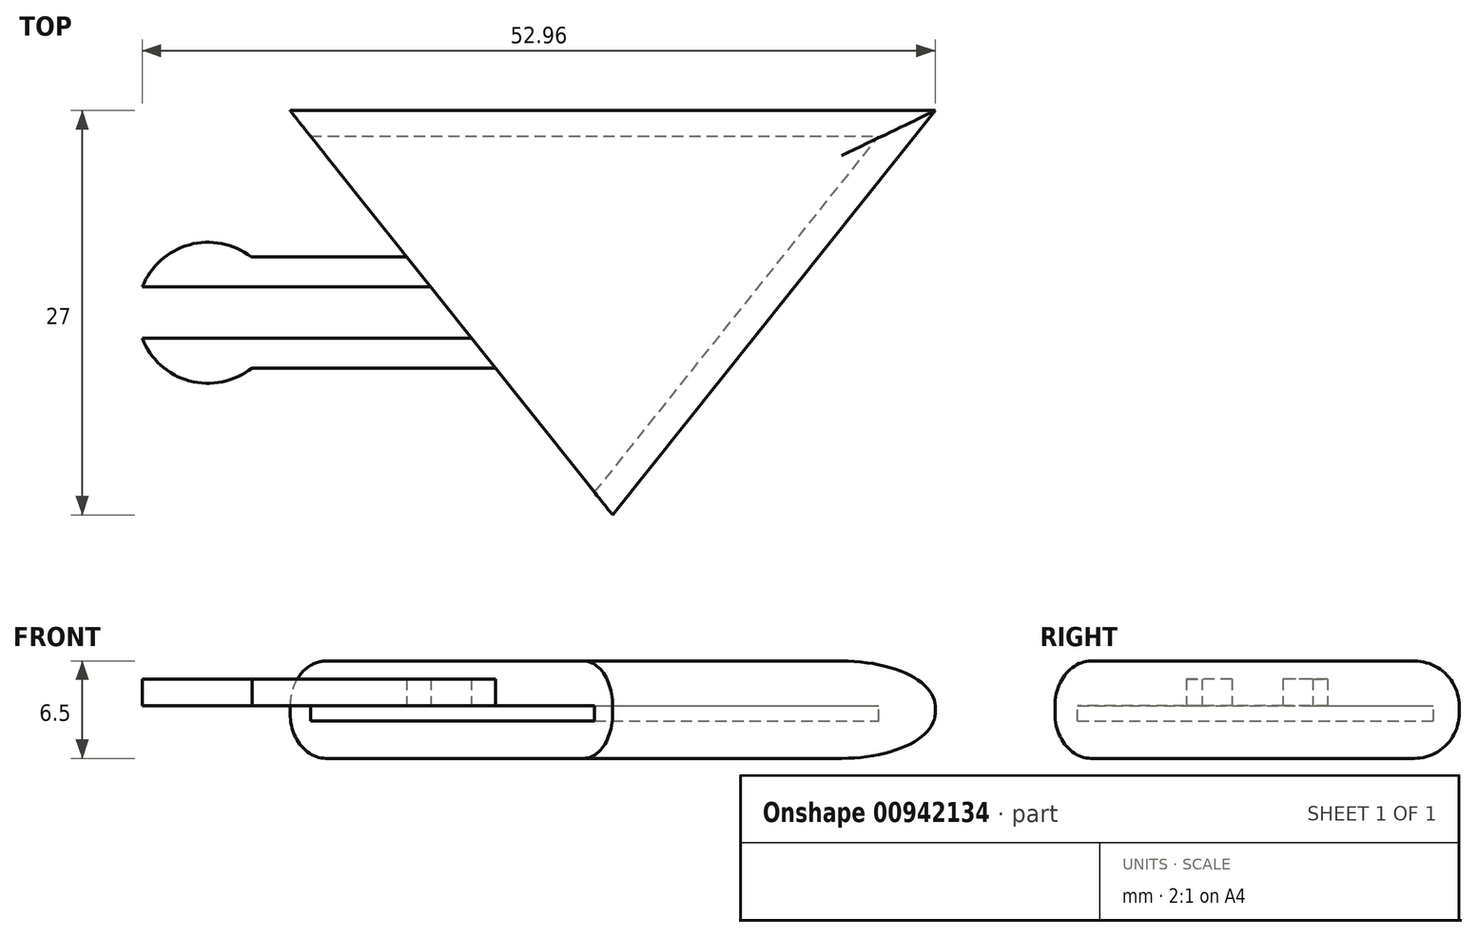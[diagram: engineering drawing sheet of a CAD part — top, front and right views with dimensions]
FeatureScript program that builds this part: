
annotation { "Feature Type Name" : "Feature", "Feature Type Description" : "" }
export const myFeature = defineFeature(function(context is Context, id is Id, definition is map)
    precondition{}
    {
        {
            var Q0;
            Q0=qCreatedBy(makeId("Top.planeOp"),FACE);
            var sketch = newSketch(context, id + "F0", { "sketchPlane" : qUnion([Q0])});
            skCircle(sketch, "E0", {"center": v(0, 0) * mm, "radius": 5 * mm, "construction": true});
            skLineSegment(sketch, "E1", {"start": v(3, 4) * mm, "end": v(13.09, 4) * mm, "construction": true});
            skLineSegment(sketch, "E2", {"start": v(3, -4) * mm, "end": v(19.42, -4) * mm, "construction": true});
            skLineSegment(sketch, "E3", {"start": v(19.42, -4) * mm, "end": v(13.09, 4) * mm, "construction": true});
            skLineSegment(sketch, "E4.MirrorCS", {"start": v(27.02, -13.5) * mm, "end": v(-5.48, -13.5) * mm, "construction": true});
            skLineSegment(sketch, "E5.MirrorCS", {"start": v(5.48, 13.5) * mm, "end": v(27.02, -13.5) * mm, "construction": true});
            skLineSegment(sketch, "E6.MirrorCS", {"start": v(-27.02, 13.5) * mm, "end": v(5.48, 13.5) * mm, "construction": true});
            skLineSegment(sketch, "E7.MirrorCS", {"start": v(-27.02, 13.5) * mm, "end": v(-5.48, -13.5) * mm, "construction": true});
            skLineSegment(sketch, "E8", {"start": v(5.48, 13.5) * mm, "end": v(48.56, 13.5) * mm, "construction": true});
            skLineSegment(sketch, "E9", {"start": v(48.56, 13.5) * mm, "end": v(27.02, -13.5) * mm, "construction": true});
            skLineSegment(sketch, "E10", {"start": v(6.85, 11.79) * mm, "end": v(44.8, 11.79) * mm, "construction": true});
            skLineSegment(sketch, "E11", {"start": v(44.8, 11.79) * mm, "end": v(25.82, -12) * mm, "construction": true});
            skSolve(sketch);
        }
        {
            var Q0;
            Q0=qCreatedBy(makeId("Top.planeOp"),FACE);
            var sketch = newSketch(context, id + "F1", { "sketchPlane" : qUnion([Q0])});
            skCircle(sketch, "E12", {"center": v(0, 0) * mm, "radius": 5 * mm, "construction": true});
            skLineSegment(sketch, "E13", {"start": v(3, 4) * mm, "end": v(13.09, 4) * mm, "construction": true});
            skLineSegment(sketch, "E14", {"start": v(3, -4) * mm, "end": v(19.42, -4) * mm, "construction": true});
            skLineSegment(sketch, "E15", {"start": v(19.42, -4) * mm, "end": v(13.09, 4) * mm, "construction": true});
            skLineSegment(sketch, "E16.MirrorCS", {"start": v(27.02, -13.5) * mm, "end": v(-5.48, -13.5) * mm, "construction": true});
            skLineSegment(sketch, "E17.MirrorCS", {"start": v(5.48, 13.5) * mm, "end": v(27.02, -13.5) * mm, "construction": true});
            skLineSegment(sketch, "E18.MirrorCS", {"start": v(-27.02, 13.5) * mm, "end": v(5.48, 13.5) * mm, "construction": true});
            skLineSegment(sketch, "E19.MirrorCS", {"start": v(-27.02, 13.5) * mm, "end": v(-5.48, -13.5) * mm, "construction": true});
            skLineSegment(sketch, "E20", {"start": v(5.48, 13.5) * mm, "end": v(48.56, 13.5) * mm, "construction": true});
            skLineSegment(sketch, "E21", {"start": v(48.56, 13.5) * mm, "end": v(27.02, -13.5) * mm, "construction": true});
            skLineSegment(sketch, "E22", {"start": v(6.85, 11.79) * mm, "end": v(44.8, 11.79) * mm, "construction": true});
            skLineSegment(sketch, "E23", {"start": v(44.8, 11.79) * mm, "end": v(25.82, -12) * mm, "construction": true});
            skLineSegment(sketch, "E24", {"start": v(5.48, 13.5) * mm, "end": v(27.02, -13.5) * mm});
            skLineSegment(sketch, "E25", {"start": v(48.56, 13.5) * mm, "end": v(5.48, 13.5) * mm});
            skLineSegment(sketch, "E26", {"start": v(48.56, 13.5) * mm, "end": v(27.02, -13.5) * mm});
            skSolve(sketch);
        }
        {
            var Q0;
            Q0=makeQuery(id+"F1.imprint","IMPRINT",FACE,{"disambiguationData":[TD([[makeQuery(id+"F1.imprint","IMPRINT",EDGE,{"derivedFrom":sQuery(id+"F1.wireOp",EDGE,"E24")}),1.0]])]});
            extrude(context, id + "F2", {"entities" : qUnion([Q0]), "oppositeDirection" : true, "depth" : 3.5 * mm, "offsetDistance" : 25 * mm});
        }
        {
            var Q0;
            Q0=qCreatedBy(makeId("Top.planeOp"),FACE);
            var sketch = newSketch(context, id + "F3", { "sketchPlane" : qUnion([Q0])});
            skCircle(sketch, "E27", {"center": v(0, 0) * mm, "radius": 5 * mm, "construction": true});
            skLineSegment(sketch, "E28", {"start": v(3, 4) * mm, "end": v(13.09, 4) * mm, "construction": true});
            skLineSegment(sketch, "E29", {"start": v(3, -4) * mm, "end": v(19.42, -4) * mm, "construction": true});
            skLineSegment(sketch, "E30", {"start": v(19.42, -4) * mm, "end": v(13.09, 4) * mm, "construction": true});
            skLineSegment(sketch, "E31.MirrorCS", {"start": v(27.02, -13.5) * mm, "end": v(-5.48, -13.5) * mm, "construction": true});
            skLineSegment(sketch, "E32.MirrorCS", {"start": v(5.48, 13.5) * mm, "end": v(27.02, -13.5) * mm, "construction": true});
            skLineSegment(sketch, "E33.MirrorCS", {"start": v(-27.02, 13.5) * mm, "end": v(5.48, 13.5) * mm, "construction": true});
            skLineSegment(sketch, "E34.MirrorCS", {"start": v(-27.02, 13.5) * mm, "end": v(-5.48, -13.5) * mm, "construction": true});
            skLineSegment(sketch, "E35", {"start": v(5.48, 13.5) * mm, "end": v(48.56, 13.5) * mm, "construction": true});
            skLineSegment(sketch, "E36", {"start": v(48.56, 13.5) * mm, "end": v(27.02, -13.5) * mm, "construction": true});
            skLineSegment(sketch, "E37", {"start": v(6.85, 11.79) * mm, "end": v(44.8, 11.79) * mm, "construction": true});
            skLineSegment(sketch, "E38", {"start": v(44.8, 11.79) * mm, "end": v(25.82, -12) * mm, "construction": true});
            skLineSegment(sketch, "E39", {"start": v(6.85, 11.79) * mm, "end": v(44.8, 11.79) * mm});
            skLineSegment(sketch, "E40", {"start": v(25.82, -12) * mm, "end": v(44.8, 11.79) * mm});
            skLineSegment(sketch, "E41", {"start": v(25.82, -12) * mm, "end": v(6.85, 11.79) * mm});
            skSolve(sketch);
        }
        {
            var Q0;
            Q0=makeQuery(id+"F3.imprint","IMPRINT",FACE,{"disambiguationData":[TD([[makeQuery(id+"F3.imprint","IMPRINT",EDGE,{"derivedFrom":sQuery(id+"F3.wireOp",EDGE,"E39")}),-1.0]])]});
            extrude(context, id + "F4", {"entities" : qUnion([Q0]), "operationType" : NewBodyOperationType.REMOVE, "oppositeDirection" : true, "depth" : 1 * mm, "offsetDistance" : 25 * mm});
        }
        {
            var Q0;
            Q0=makeQuery(id+"F2.opExtrude","CAP_FACE",FACE,{"disambiguationData":[OSD([sQuery(id+"F1.wireOp",EDGE,"E24"),sQuery(id+"F1.wireOp",EDGE,"E25"),sQuery(id+"F1.wireOp",EDGE,"E26")])],"isStart":true});
            var sketch = newSketch(context, id + "F5", { "sketchPlane" : qUnion([Q0])});
            skCircle(sketch, "E42", {"center": v(0, 0) * mm, "radius": 5 * mm, "construction": true});
            skLineSegment(sketch, "E43", {"start": v(3, 4) * mm, "end": v(13.09, 4) * mm, "construction": true});
            skLineSegment(sketch, "E44", {"start": v(3, -4) * mm, "end": v(19.42, -4) * mm, "construction": true});
            skLineSegment(sketch, "E45", {"start": v(19.42, -4) * mm, "end": v(13.09, 4) * mm, "construction": true});
            skLineSegment(sketch, "E46.MirrorCS", {"start": v(27.02, -13.5) * mm, "end": v(-5.48, -13.5) * mm, "construction": true});
            skLineSegment(sketch, "E47.MirrorCS", {"start": v(5.48, 13.5) * mm, "end": v(27.02, -13.5) * mm, "construction": true});
            skLineSegment(sketch, "E48.MirrorCS", {"start": v(-27.02, 13.5) * mm, "end": v(5.48, 13.5) * mm, "construction": true});
            skLineSegment(sketch, "E49.MirrorCS", {"start": v(-27.02, 13.5) * mm, "end": v(-5.48, -13.5) * mm, "construction": true});
            skLineSegment(sketch, "E50", {"start": v(5.48, 13.5) * mm, "end": v(48.56, 13.5) * mm, "construction": true});
            skLineSegment(sketch, "E51", {"start": v(48.56, 13.5) * mm, "end": v(27.02, -13.5) * mm, "construction": true});
            skLineSegment(sketch, "E52", {"start": v(6.85, 11.79) * mm, "end": v(44.8, 11.79) * mm, "construction": true});
            skLineSegment(sketch, "E53", {"start": v(44.8, 11.79) * mm, "end": v(25.82, -12) * mm, "construction": true});
            skCircle(sketch, "E54", {"center": v(0, 0) * mm, "radius": 4.71 * mm});
            skLineSegment(sketch, "E55", {"start": v(2.88, 3.73) * mm, "end": v(13.28, 3.73) * mm});
            skLineSegment(sketch, "E56", {"start": v(2.93, -3.69) * mm, "end": v(19.2, -3.69) * mm});
            skLineSegment(sketch, "E57", {"start": v(9.17, -3.69) * mm, "end": v(9.17, -1.69) * mm, "construction": true});
            skLineSegment(sketch, "E58", {"start": v(8.08, 3.73) * mm, "end": v(8.08, 1.73) * mm, "construction": true});
            skLineSegment(sketch, "E59", {"start": v(14.87, 1.73) * mm, "end": v(4.38, 1.73) * mm});
            skLineSegment(sketch, "E60", {"start": v(4.38, 1.73) * mm, "end": v(-4.38, 1.73) * mm});
            skLineSegment(sketch, "E61", {"start": v(17.6, -1.69) * mm, "end": v(4.4, -1.69) * mm});
            skLineSegment(sketch, "E62", {"start": v(4.4, -1.69) * mm, "end": v(-4.4, -1.69) * mm});
            skLineSegment(sketch, "E63", {"start": v(13.28, 3.73) * mm, "end": v(5.48, 13.5) * mm});
            skLineSegment(sketch, "E64", {"start": v(48.56, 13.5) * mm, "end": v(27.02, -13.5) * mm});
            skLineSegment(sketch, "E65", {"start": v(19.2, -3.69) * mm, "end": v(27.02, -13.5) * mm});
            skLineSegment(sketch, "E66", {"start": v(14.87, 1.73) * mm, "end": v(17.6, -1.69) * mm});
            skSolve(sketch);
        }
        {
            var Q0;
            {var subQ2=sQuery(id+"F5.wireOp",EDGE,"E55");Q0=makeQuery(id+"F5.imprint","IMPRINT",FACE,{"disambiguationData":[TD([[makeQuery(id+"F5.imprint","IMPRINT",EDGE,{"derivedFrom":subQ2}),-1.0]])]});}
            var Q1;
            {var subQ2=sQuery(id+"F5.wireOp",EDGE,"E64");Q1=makeQuery(id+"F5.imprint","IMPRINT",FACE,{"disambiguationData":[TD([[makeQuery(id+"F5.imprint","IMPRINT",EDGE,{"derivedFrom":subQ2}),-1.0]])]});}
            var Q2;
            {var subQ2=sQuery(id+"F5.wireOp",EDGE,"E60");Q2=makeQuery(id+"F5.imprint","IMPRINT",FACE,{"disambiguationData":[TD([[makeQuery(id+"F5.imprint","IMPRINT",EDGE,{"derivedFrom":subQ2}),-1.0]])]});}
            var Q3;
            {var subQ2=sQuery(id+"F5.wireOp",EDGE,"E62");Q3=makeQuery(id+"F5.imprint","IMPRINT",FACE,{"disambiguationData":[TD([[makeQuery(id+"F5.imprint","IMPRINT",EDGE,{"derivedFrom":subQ2}),1.0]])]});}
            extrude(context, id + "F6", {"entities" : qUnion([Q0, Q1, Q2, Q3]), "operationType" : NewBodyOperationType.ADD, "depth" : 1.8 * mm, "offsetDistance" : 25 * mm});
        }
        {
            var Q0;
            Q0=makeQuery(id+"F6.opExtrude","CAP_FACE",FACE,{"disambiguationData":[OSD([sQuery(id+"F1.wireOp",EDGE,"E25"),sQuery(id+"F5.wireOp",EDGE,"E54"),sQuery(id+"F5.wireOp",EDGE,"E55"),sQuery(id+"F5.wireOp",EDGE,"E56"),sQuery(id+"F5.wireOp",EDGE,"E59"),sQuery(id+"F5.wireOp",EDGE,"E60"),sQuery(id+"F5.wireOp",EDGE,"E61"),sQuery(id+"F5.wireOp",EDGE,"E62"),sQuery(id+"F5.wireOp",EDGE,"E63"),sQuery(id+"F5.wireOp",EDGE,"E64"),sQuery(id+"F5.wireOp",EDGE,"E65"),sQuery(id+"F5.wireOp",EDGE,"E66")])],"isStart":false});
            var sketch = newSketch(context, id + "F7", { "sketchPlane" : qUnion([Q0])});
            skCircle(sketch, "E67", {"center": v(0, 0) * mm, "radius": 5 * mm, "construction": true});
            skLineSegment(sketch, "E68", {"start": v(3, 4) * mm, "end": v(13.09, 4) * mm, "construction": true});
            skLineSegment(sketch, "E69", {"start": v(3, -4) * mm, "end": v(19.42, -4) * mm, "construction": true});
            skLineSegment(sketch, "E70", {"start": v(19.42, -4) * mm, "end": v(13.09, 4) * mm, "construction": true});
            skLineSegment(sketch, "E71.MirrorCS", {"start": v(27.02, -13.5) * mm, "end": v(-5.48, -13.5) * mm, "construction": true});
            skLineSegment(sketch, "E72.MirrorCS", {"start": v(5.48, 13.5) * mm, "end": v(27.02, -13.5) * mm, "construction": true});
            skLineSegment(sketch, "E73.MirrorCS", {"start": v(-27.02, 13.5) * mm, "end": v(5.48, 13.5) * mm, "construction": true});
            skLineSegment(sketch, "E74.MirrorCS", {"start": v(-27.02, 13.5) * mm, "end": v(-5.48, -13.5) * mm, "construction": true});
            skLineSegment(sketch, "E75", {"start": v(5.48, 13.5) * mm, "end": v(48.56, 13.5) * mm, "construction": true});
            skLineSegment(sketch, "E76", {"start": v(48.56, 13.5) * mm, "end": v(27.02, -13.5) * mm, "construction": true});
            skLineSegment(sketch, "E77", {"start": v(6.85, 11.79) * mm, "end": v(44.8, 11.79) * mm, "construction": true});
            skLineSegment(sketch, "E78", {"start": v(44.8, 11.79) * mm, "end": v(25.82, -12) * mm, "construction": true});
            skLineSegment(sketch, "E79", {"start": v(5.48, 13.5) * mm, "end": v(27.02, -13.5) * mm});
            skLineSegment(sketch, "E80", {"start": v(48.56, 13.5) * mm, "end": v(5.48, 13.5) * mm});
            skSolve(sketch);
        }
        {
            var Q0;
            {var subQ4=sQuery(id+"F7.wireOp",EDGE,"E80");Q0=makeQuery(id+"F7.imprint","IMPRINT",FACE,{"disambiguationData":[TD([[makeQuery(id+"F7.imprint","IMPRINT",EDGE,{"derivedFrom":subQ4}),1.0]])]});}
            extrude(context, id + "F8", {"entities" : qUnion([Q0]), "operationType" : NewBodyOperationType.ADD, "depth" : 1.2 * mm, "offsetDistance" : 25 * mm});
        }
        {
            var Q0;
            Q0=makeQuery(id+"F8.opExtrude","CAP_EDGE",EDGE,{"disambiguationData":[OSD([sQuery(id+"F7.wireOp",EDGE,"E80")])],"isStart":false});
            var Q1;
            Q1=makeQuery(id+"F2.opExtrude","CAP_EDGE",EDGE,{"disambiguationData":[OSD([sQuery(id+"F1.wireOp",EDGE,"E25")])],"isStart":false});
            var Q2;
            Q2=makeQuery(id+"F8.opExtrude","CAP_EDGE",EDGE,{"disambiguationData":[OSD([sQuery(id+"F5.wireOp",EDGE,"E64")])],"isStart":false});
            var Q3;
            Q3=makeQuery(id+"F2.opExtrude","CAP_EDGE",EDGE,{"disambiguationData":[OSD([sQuery(id+"F1.wireOp",EDGE,"E26")])],"isStart":false});
            fillet(context, id + "F9", {"entities" : qUnion([Q0, Q1, Q2, Q3]), "radius" : 3 * mm, "tangentPropagation" : true, "allowEdgeOverflow" : false});
        }
    });
